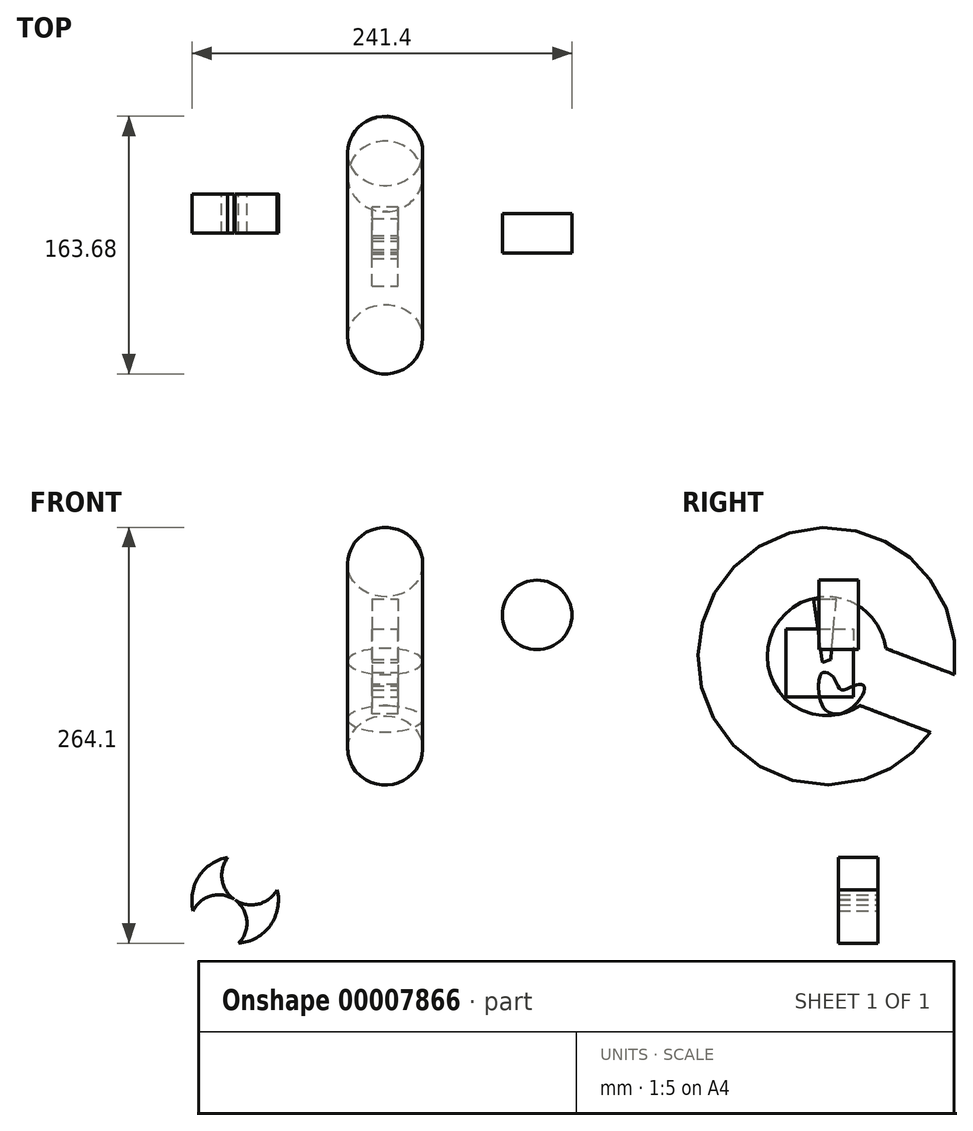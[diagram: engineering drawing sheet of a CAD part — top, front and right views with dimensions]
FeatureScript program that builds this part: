
annotation { "Feature Type Name" : "Feature", "Feature Type Description" : "" }
export const myFeature = defineFeature(function(context is Context, id is Id, definition is map)
    precondition{}
    {
        {
            var Q0;
            Q0=qCreatedBy(makeId("Right.planeOp"),FACE);
            var sketch = newSketch(context, id + "F0", { "sketchPlane" : qUnion([Q0])});
            skLineSegment(sketch, "E0", {"start": v(19.95, -37.15) * mm, "end": v(-30.55, -17.84) * mm});
            skLineSegment(sketch, "E1", {"start": v(-30.55, -17.84) * mm, "end": v(-20, 20.6) * mm});
            skLineSegment(sketch, "E2", {"start": v(-20, 20.6) * mm, "end": v(30.51, 1.3) * mm});
            skLineSegment(sketch, "E3", {"start": v(30.51, 1.3) * mm, "end": v(19.95, -37.15) * mm});
            skSolve(sketch);
        }
        {
            var Q0;
            Q0=makeQuery(id+"F0.imprint","IMPRINT",FACE,{"disambiguationData":[TD([[makeQuery(id+"F0.imprint","IMPRINT",EDGE,{"derivedFrom":sQuery(id+"F0.wireOp",EDGE,"E0")}),-1.0]])]});
            extrude(context, id + "F1", {"entities" : qUnion([Q0]), "depth" : 50.8 * mm});
        }
        {
            var Q0;
            Q0=qCreatedBy(makeId("Top.planeOp"),FACE);
            var sketch = newSketch(context, id + "F2", { "sketchPlane" : qUnion([Q0])});
            skCircle(sketch, "E4", {"center": v(-26.99, 35.44) * mm, "radius": 23.77 * mm});
            skSolve(sketch);
        }
        {
            var Q0;
            Q0=makeQuery(id+"F2.imprint","IMPRINT",FACE,{"disambiguationData":[TD([[makeQuery(id+"F2.imprint","IMPRINT",EDGE,{"derivedFrom":sQuery(id+"F2.wireOp",EDGE,"E4")}),1.0]])]});
            var Q1;
            Q1=makeQuery(id+"F1.opExtrude","SWEPT_EDGE",EDGE,{"disambiguationData":[OSD([sQuery(id+"F0.wireOp",EDGE,"E1"),sQuery(id+"F0.wireOp",EDGE,"E2")])]});
            revolve(context, id + "F3", {"entities" : qUnion([Q0]), "axis" : qUnion([Q1]), "revolveType" : RevolveType.FULL});
        }
        {
            var Q0;
            Q0=makeQuery(id+"F1.opExtrude","SWEPT_BODY",BODY,{"disambiguationData":[OSD([sQuery(id+"F0.wireOp",EDGE,"E0"),sQuery(id+"F0.wireOp",EDGE,"E1"),sQuery(id+"F0.wireOp",EDGE,"E2"),sQuery(id+"F0.wireOp",EDGE,"E3")])]});
            var Q1;
            Q1=sQuery(id+"F0.wireOp",VERTEX,"E0.start");
            var Q2;
            Q2=makeQuery(id+"F1.opExtrude","CAP_VERTEX",VERTEX,{"disambiguationData":[OSD([sQuery(id+"F0.wireOp",EDGE,"E1"),sQuery(id+"F0.wireOp",EDGE,"E2")])],"isStart":false});
            transform(context, id + "F4", {"entities" : qUnion([Q0]), "transformType" : TransformType.TRANSLATION_ENTITY, "oppositeDirectionEntity" : true, "transformLine" : qUnion([Q1, Q2]), "makeCopy" : false});
        }
        {
            var Q0;
            Q0=makeQuery(id+"F1.opExtrude","SWEPT_BODY",BODY,{"disambiguationData":[OSD([sQuery(id+"F0.wireOp",EDGE,"E0"),sQuery(id+"F0.wireOp",EDGE,"E1"),sQuery(id+"F0.wireOp",EDGE,"E2"),sQuery(id+"F0.wireOp",EDGE,"E3")])]});
            var Q1;
            Q1=makeQuery(id+"F1.opExtrude","CAP_VERTEX",VERTEX,{"disambiguationData":[OSD([sQuery(id+"F0.wireOp",EDGE,"E0"),sQuery(id+"F0.wireOp",EDGE,"E3")])],"isStart":true});
            var Q2;
            Q2=makeQuery(id+"F1.opExtrude","CAP_VERTEX",VERTEX,{"disambiguationData":[OSD([sQuery(id+"F0.wireOp",EDGE,"E1"),sQuery(id+"F0.wireOp",EDGE,"E2")])],"isStart":true});
            transform(context, id + "F5", {"entities" : qUnion([Q0]), "transformType" : TransformType.TRANSLATION_ENTITY, "oppositeDirectionEntity" : false, "transformLine" : qUnion([Q1, Q2]), "makeCopy" : false});
        }
        {
            var Q0;
            Q0=makeQuery(id+"F1.opExtrude","SWEPT_BODY",BODY,{"disambiguationData":[OSD([sQuery(id+"F0.wireOp",EDGE,"E0"),sQuery(id+"F0.wireOp",EDGE,"E1"),sQuery(id+"F0.wireOp",EDGE,"E2"),sQuery(id+"F0.wireOp",EDGE,"E3")])]});
            transform(context, id + "F6", {"entities" : qUnion([Q0]), "transformType" : TransformType.TRANSLATION_3D, "dx" : 0 * mm, "dy" : 31.82 * mm, "dz" : 7.18 * mm, "makeCopy" : false});
        }
        {
            var Q0;
            Q0=makeQuery(id+"F1.opExtrude","SWEPT_BODY",BODY,{"disambiguationData":[OSD([sQuery(id+"F0.wireOp",EDGE,"E0"),sQuery(id+"F0.wireOp",EDGE,"E1"),sQuery(id+"F0.wireOp",EDGE,"E2"),sQuery(id+"F0.wireOp",EDGE,"E3")])]});
            var Q1;
            Q1=makeQuery(id+"F3.opRevolve","SWEPT_BODY",BODY,{"disambiguationData":[OSD([sQuery(id+"F2.wireOp",EDGE,"E4")])]});
            booleanBodies(context, id + "F7", {"operationType" : BooleanOperationType.SUBTRACTION, "tools" : qUnion([Q0]), "targets" : qUnion([Q1])});
        }
        {
            var Q0;
            Q0=qCreatedBy(makeId("Front.planeOp"),FACE);
            var sketch = newSketch(context, id + "F8", { "sketchPlane" : qUnion([Q0])});
            skLineSegment(sketch, "E5", {"start": v(122.05, 43.72) * mm, "end": v(113.3, -18.18) * mm});
            skLineSegment(sketch, "E6", {"start": v(105.23, -15.49) * mm, "end": v(99.7, 43.72) * mm});
            skLineSegment(sketch, "E7", {"start": v(105.23, -15.49) * mm, "end": v(113.3, -18.18) * mm});
            skLineSegment(sketch, "E8", {"start": v(122.05, 43.72) * mm, "end": v(99.7, 43.72) * mm});
            skLineSegment(sketch, "E9.bottom", {"start": v(148.96, 14.45) * mm, "end": v(83.03, 14.45) * mm});
            skLineSegment(sketch, "E9.top", {"start": v(148.96, -51.82) * mm, "end": v(83.03, -51.82) * mm});
            skLineSegment(sketch, "E9.left", {"start": v(148.96, 14.45) * mm, "end": v(148.96, -51.82) * mm});
            skLineSegment(sketch, "E9.right", {"start": v(83.03, 14.45) * mm, "end": v(83.03, -51.82) * mm});
            skFitSpline(sketch, "E10", {"points": [v(117, -38.38) * mm, v(111.6, -63.46) * mm, v(89.21, -65.78) * mm, v(72.23, -42.62) * mm, v(79.18, -39.92) * mm, v(95, -44.94) * mm, v(102.72, -32.6) * mm, v(113.52, -28.35) * mm, v(116.22, -33.36) * mm, v(117, -38.38) * mm]});
            skSolve(sketch);
        }
        {
            var Q0;
            {var subQ5=sQuery(id+"F8.wireOp",EDGE,"E8");Q0=makeQuery(id+"F8.imprint","IMPRINT",FACE,{"disambiguationData":[TD([[makeQuery(id+"F8.imprint","IMPRINT",EDGE,{"derivedFrom":subQ5}),1.0]])]});}
            var Q1;
            {var subQ7=sQuery(id+"F8.wireOp",EDGE,"E7");Q1=makeQuery(id+"F8.imprint","IMPRINT",FACE,{"disambiguationData":[TD([[makeQuery(id+"F8.imprint","IMPRINT",EDGE,{"derivedFrom":subQ7}),-1.0]])]});}
            var Q2;
            {var subQ1=sQuery(id+"F8.wireOp",EDGE,"E9.right");var subQ3=sQuery(id+"F8.wireOp",EDGE,"E9.top");var subQ5=makeQuery(id+"F8.imprint","INTERSECT",VERTEX,{"derivedFrom":[subQ3,subQ1]});Q2=makeQuery(id+"F8.imprint","IMPRINT",FACE,{"disambiguationData":[TD([[makeQuery(id+"F8.imprint","IMPRINT",EDGE,{"disambiguationData":[TD([[subQ5,1.0]])],"derivedFrom":subQ3}),1.0]])]});}
            extrude(context, id + "F9", {"entities" : qUnion([Q0, Q1, Q2]), "depth" : 25.4 * mm});
        }
        {
            var Q0;
            Q0=makeQuery(id+"F9.opExtrude","SWEPT_BODY",BODY,{"disambiguationData":[OSD([sQuery(id+"F8.wireOp",EDGE,"E5"),sQuery(id+"F8.wireOp",EDGE,"E6"),sQuery(id+"F8.wireOp",EDGE,"E7"),sQuery(id+"F8.wireOp",EDGE,"E9.bottom"),sQuery(id+"F8.wireOp",EDGE,"E9.top"),sQuery(id+"F8.wireOp",EDGE,"E9.left"),sQuery(id+"F8.wireOp",EDGE,"E9.right"),sQuery(id+"F8.wireOp",EDGE,"E10")])]});
            var Q1;
            Q1=makeQuery(id+"F9.opExtrude","SWEPT_BODY",BODY,{"disambiguationData":[OSD([sQuery(id+"F8.wireOp",EDGE,"E9.top"),sQuery(id+"F8.wireOp",EDGE,"E9.right"),sQuery(id+"F8.wireOp",EDGE,"E10")])]});
            var Q2;
            Q2=makeQuery(id+"F9.opExtrude","SWEPT_BODY",BODY,{"disambiguationData":[OSD([sQuery(id+"F8.wireOp",EDGE,"E5"),sQuery(id+"F8.wireOp",EDGE,"E6"),sQuery(id+"F8.wireOp",EDGE,"E8"),sQuery(id+"F8.wireOp",EDGE,"E9.bottom")])]});
            var Q3;
            Q3=makeQuery(id+"F9.opExtrude","CAP_EDGE",EDGE,{"disambiguationData":[OSD([sQuery(id+"F8.wireOp",EDGE,"E9.left")])],"isStart":false});
            transform(context, id + "F10", {"entities" : qUnion([Q0, Q1, Q2]), "transformType" : TransformType.ROTATION, "transformAxis" : qUnion([Q3]), "angle" : 90 * degree, "makeCopy" : false});
        }
        {
            var Q0;
            Q0=makeQuery(id+"F9.opExtrude","SWEPT_BODY",BODY,{"disambiguationData":[OSD([sQuery(id+"F8.wireOp",EDGE,"E9.top"),sQuery(id+"F8.wireOp",EDGE,"E9.right"),sQuery(id+"F8.wireOp",EDGE,"E10")])]});
            var Q1;
            Q1=makeQuery(id+"F9.opExtrude","SWEPT_BODY",BODY,{"disambiguationData":[OSD([sQuery(id+"F8.wireOp",EDGE,"E5"),sQuery(id+"F8.wireOp",EDGE,"E6"),sQuery(id+"F8.wireOp",EDGE,"E7"),sQuery(id+"F8.wireOp",EDGE,"E9.bottom"),sQuery(id+"F8.wireOp",EDGE,"E9.top"),sQuery(id+"F8.wireOp",EDGE,"E9.left"),sQuery(id+"F8.wireOp",EDGE,"E9.right"),sQuery(id+"F8.wireOp",EDGE,"E10")])]});
            var Q2;
            Q2=makeQuery(id+"F9.opExtrude","SWEPT_BODY",BODY,{"disambiguationData":[OSD([sQuery(id+"F8.wireOp",EDGE,"E5"),sQuery(id+"F8.wireOp",EDGE,"E6"),sQuery(id+"F8.wireOp",EDGE,"E8"),sQuery(id+"F8.wireOp",EDGE,"E9.bottom")])]});
            transform(context, id + "F11", {"entities" : qUnion([Q0, Q1, Q2]), "transformType" : TransformType.TRANSLATION_3D, "dx" : 0 * mm, "dy" : -32.97 * mm, "dz" : 32.3 * mm, "makeCopy" : false});
        }
        {
            var Q0;
            Q0=makeQuery(id+"F9.opExtrude","SWEPT_BODY",BODY,{"disambiguationData":[OSD([sQuery(id+"F8.wireOp",EDGE,"E9.top"),sQuery(id+"F8.wireOp",EDGE,"E9.right"),sQuery(id+"F8.wireOp",EDGE,"E10")])]});
            var Q1;
            Q1=makeQuery(id+"F9.opExtrude","SWEPT_BODY",BODY,{"disambiguationData":[OSD([sQuery(id+"F8.wireOp",EDGE,"E5"),sQuery(id+"F8.wireOp",EDGE,"E6"),sQuery(id+"F8.wireOp",EDGE,"E7"),sQuery(id+"F8.wireOp",EDGE,"E9.bottom"),sQuery(id+"F8.wireOp",EDGE,"E9.top"),sQuery(id+"F8.wireOp",EDGE,"E9.left"),sQuery(id+"F8.wireOp",EDGE,"E9.right"),sQuery(id+"F8.wireOp",EDGE,"E10")])]});
            var Q2;
            Q2=makeQuery(id+"F9.opExtrude","SWEPT_BODY",BODY,{"disambiguationData":[OSD([sQuery(id+"F8.wireOp",EDGE,"E5"),sQuery(id+"F8.wireOp",EDGE,"E6"),sQuery(id+"F8.wireOp",EDGE,"E8"),sQuery(id+"F8.wireOp",EDGE,"E9.bottom")])]});
            var Q3;
            Q3=makeQuery(id+"F9.opExtrude","CAP_VERTEX",VERTEX,{"disambiguationData":[OSD([sQuery(id+"F8.wireOp",EDGE,"E5"),sQuery(id+"F8.wireOp",EDGE,"E7")])],"isStart":true});
            transform(context, id + "F12", {"entities" : qUnion([Q0, Q1, Q2]), "transformType" : TransformType.SCALE_UNIFORMLY, "scale" : 0.65, "makeCopy" : false, "scalePoint" : qUnion([Q3])});
        }
        {
            var Q0;
            Q0=makeQuery(id+"F9.opExtrude","SWEPT_BODY",BODY,{"disambiguationData":[OSD([sQuery(id+"F8.wireOp",EDGE,"E9.top"),sQuery(id+"F8.wireOp",EDGE,"E9.right"),sQuery(id+"F8.wireOp",EDGE,"E10")])]});
            var Q1;
            Q1=makeQuery(id+"F9.opExtrude","SWEPT_BODY",BODY,{"disambiguationData":[OSD([sQuery(id+"F8.wireOp",EDGE,"E5"),sQuery(id+"F8.wireOp",EDGE,"E6"),sQuery(id+"F8.wireOp",EDGE,"E7"),sQuery(id+"F8.wireOp",EDGE,"E9.bottom"),sQuery(id+"F8.wireOp",EDGE,"E9.top"),sQuery(id+"F8.wireOp",EDGE,"E9.left"),sQuery(id+"F8.wireOp",EDGE,"E9.right"),sQuery(id+"F8.wireOp",EDGE,"E10")])]});
            var Q2;
            Q2=makeQuery(id+"F9.opExtrude","SWEPT_BODY",BODY,{"disambiguationData":[OSD([sQuery(id+"F8.wireOp",EDGE,"E5"),sQuery(id+"F8.wireOp",EDGE,"E6"),sQuery(id+"F8.wireOp",EDGE,"E8"),sQuery(id+"F8.wireOp",EDGE,"E9.bottom")])]});
            transform(context, id + "F13", {"entities" : qUnion([Q0, Q1, Q2]), "transformType" : TransformType.TRANSLATION_3D, "dx" : 0 * mm, "dy" : 0 * mm, "dz" : 2.7 * mm, "makeCopy" : false});
        }
        {
            var Q0;
            Q0=makeQuery(id+"F9.opExtrude","SWEPT_BODY",BODY,{"disambiguationData":[OSD([sQuery(id+"F8.wireOp",EDGE,"E9.top"),sQuery(id+"F8.wireOp",EDGE,"E9.right"),sQuery(id+"F8.wireOp",EDGE,"E10")])]});
            var Q1;
            Q1=makeQuery(id+"F9.opExtrude","SWEPT_BODY",BODY,{"disambiguationData":[OSD([sQuery(id+"F8.wireOp",EDGE,"E5"),sQuery(id+"F8.wireOp",EDGE,"E6"),sQuery(id+"F8.wireOp",EDGE,"E8"),sQuery(id+"F8.wireOp",EDGE,"E9.bottom")])]});
            var Q2;
            Q2=makeQuery(id+"F9.opExtrude","SWEPT_BODY",BODY,{"disambiguationData":[OSD([sQuery(id+"F8.wireOp",EDGE,"E5"),sQuery(id+"F8.wireOp",EDGE,"E6"),sQuery(id+"F8.wireOp",EDGE,"E7"),sQuery(id+"F8.wireOp",EDGE,"E9.bottom"),sQuery(id+"F8.wireOp",EDGE,"E9.top"),sQuery(id+"F8.wireOp",EDGE,"E9.left"),sQuery(id+"F8.wireOp",EDGE,"E9.right"),sQuery(id+"F8.wireOp",EDGE,"E10")])]});
            var Q3;
            {var subQ0=sQuery(id+"F8.wireOp",EDGE,"E9.right");var subQ1=sQuery(id+"F8.wireOp",EDGE,"E10");Q3=makeQuery(id+"F9.opExtrude","CAP_VERTEX",VERTEX,{"disambiguationData":[OSD([subQ0,subQ1]),ownerDisambiguation([makeQuery(id+"F9.opExtrude","SWEPT_BODY",BODY,{"disambiguationData":[OSD([sQuery(id+"F8.wireOp",EDGE,"E5"),sQuery(id+"F8.wireOp",EDGE,"E6"),sQuery(id+"F8.wireOp",EDGE,"E7"),sQuery(id+"F8.wireOp",EDGE,"E9.bottom"),sQuery(id+"F8.wireOp",EDGE,"E9.top"),sQuery(id+"F8.wireOp",EDGE,"E9.left"),subQ0,subQ1])]})])],"isStart":false});}
            transform(context, id + "F14", {"entities" : qUnion([Q0, Q1, Q2]), "transformType" : TransformType.TRANSLATION_3D, "dx" : -191.07 * mm, "dy" : 0 * mm, "dz" : 0 * mm, "makeCopy" : false});
        }
        {
            var Q0;
            Q0=makeQuery(id+"F9.opExtrude","SWEPT_BODY",BODY,{"disambiguationData":[OSD([sQuery(id+"F8.wireOp",EDGE,"E5"),sQuery(id+"F8.wireOp",EDGE,"E6"),sQuery(id+"F8.wireOp",EDGE,"E7"),sQuery(id+"F8.wireOp",EDGE,"E9.bottom"),sQuery(id+"F8.wireOp",EDGE,"E9.top"),sQuery(id+"F8.wireOp",EDGE,"E9.left"),sQuery(id+"F8.wireOp",EDGE,"E9.right"),sQuery(id+"F8.wireOp",EDGE,"E10")])]});
            var Q1;
            Q1=makeQuery(id+"F9.opExtrude","SWEPT_BODY",BODY,{"disambiguationData":[OSD([sQuery(id+"F8.wireOp",EDGE,"E5"),sQuery(id+"F8.wireOp",EDGE,"E6"),sQuery(id+"F8.wireOp",EDGE,"E8"),sQuery(id+"F8.wireOp",EDGE,"E9.bottom")])]});
            var Q2;
            Q2=makeQuery(id+"F9.opExtrude","SWEPT_BODY",BODY,{"disambiguationData":[OSD([sQuery(id+"F8.wireOp",EDGE,"E9.top"),sQuery(id+"F8.wireOp",EDGE,"E9.right"),sQuery(id+"F8.wireOp",EDGE,"E10")])]});
            transform(context, id + "F15", {"entities" : qUnion([Q0, Q1, Q2]), "transformType" : TransformType.TRANSLATION_3D, "dx" : -2.02 * mm, "dy" : 0 * mm, "dz" : 0 * mm, "makeCopy" : false});
        }
        {
            var Q0;
            Q0=qCreatedBy(makeId("Front.planeOp"),FACE);
            var sketch = newSketch(context, id + "F16", { "sketchPlane" : qUnion([Q0])});
            skEllipse(sketch, "E11", {"center": v(132.43, 37.26) * mm, "majorRadius": 10 * mm, "minorRadius": 6.2 * mm, "majorAxis": v(-0.77, 0.64)});
            skCircle(sketch, "E12", {"center": v(69.53, 46.9) * mm, "radius": 12.85 * mm});
            skCircle(sketch, "E13", {"center": v(69.53, 46.9) * mm, "radius": 22.07 * mm});
            skArc(sketch, "E14", {"start": v(-10.98, -133.24) * mm, "mid": v(4.84, -158.05) * mm, "end": v(34.14, -155.42) * mm});
            skArc(sketch, "E15", {"start": v(34.14, -155.42) * mm, "mid": v(29.82, -107.24) * mm, "end": v(-10.98, -133.24) * mm});
            skLineSegment(sketch, "E16", {"start": v(-10.98, -133.24) * mm, "end": v(34.14, -155.42) * mm});
            skLineSegment(sketch, "E17", {"start": v(17.33, -104.33) * mm, "end": v(17.33, -132.64) * mm});
            skLineSegment(sketch, "E18", {"start": v(17.33, -132.64) * mm, "end": v(42.01, -146.51) * mm});
            skArc(sketch, "E19.0", {"start": v(-22.97, -133.49) * mm, "mid": v(-0.46, -168.82) * mm, "end": v(41.27, -165.08) * mm});
            skLineSegment(sketch, "E20", {"start": v(-10.98, -133.24) * mm, "end": v(-22.97, -133.49) * mm});
            skLineSegment(sketch, "E21", {"start": v(34.14, -155.42) * mm, "end": v(41.27, -165.08) * mm});
            skSolve(sketch);
        }
        {
            var Q0;
            Q0=makeQuery(id+"F16.imprint","IMPRINT",FACE,{"disambiguationData":[TD([[makeQuery(id+"F16.imprint","IMPRINT",EDGE,{"derivedFrom":sQuery(id+"F16.wireOp",EDGE,"E12")}),1.0]])]});
            var Q1;
            Q1=makeQuery(id+"F16.imprint","IMPRINT",FACE,{"disambiguationData":[TD([[makeQuery(id+"F16.imprint","IMPRINT",EDGE,{"derivedFrom":sQuery(id+"F16.wireOp",EDGE,"E12")}),-1.0]])]});
            var Q2;
            Q2=sQuery(id+"F16.wireOp",EDGE,"E13");
            var Q3;
            Q3=sQuery(id+"F16.wireOp",EDGE,"E12");
            extrude(context, id + "F17", {"entities" : qUnion([Q0, Q1]), "surfaceEntities" : qUnion([Q2, Q3]), "depth" : 25 * mm});
        }
        {
            var Q0;
            Q0=qCreatedBy(makeId("Front.planeOp"),FACE);
            var sketch = newSketch(context, id + "F18", { "sketchPlane" : qUnion([Q0])});
            skCircle(sketch, "E22", {"center": v(-112.01, -118.53) * mm, "radius": 18.79 * mm});
            skArc(sketch, "E23", {"start": v(-126.96, -107.15) * mm, "mid": v(-137.35, -157.26) * mm, "end": v(-95.6, -127.67) * mm});
            skArc(sketch, "E24", {"start": v(-120.02, -161.66) * mm, "mid": v(-122.3, -134.25) * mm, "end": v(-148.96, -140.97) * mm});
            skLineSegment(sketch, "E25", {"start": v(-112.01, -118.53) * mm, "end": v(-112.01, -98.92) * mm, "construction": true});
            skSolve(sketch);
        }
        {
            var Q0;
            {var subQ1=sQuery(id+"F18.wireOp",EDGE,"E22");var subQ3=sQuery(id+"F18.wireOp",EDGE,"E23");var subQ5=makeQuery(id+"F18.imprint","INTERSECT",VERTEX,{"disambiguationData":[OD(0.0)],"derivedFrom":[subQ1,subQ3]});Q0=makeQuery(id+"F18.imprint","IMPRINT",FACE,{"disambiguationData":[TD([[makeQuery(id+"F18.imprint","IMPRINT",EDGE,{"disambiguationData":[TD([[subQ5,-1.0]])],"derivedFrom":subQ1}),-1.0]])]});}
            var Q1;
            {var subQ1=sQuery(id+"F18.wireOp",EDGE,"E22");var subQ3=sQuery(id+"F18.wireOp",EDGE,"E23");var subQ5=makeQuery(id+"F18.imprint","INTERSECT",VERTEX,{"disambiguationData":[OD(1.0)],"derivedFrom":[subQ1,subQ3]});Q1=makeQuery(id+"F18.imprint","IMPRINT",FACE,{"disambiguationData":[TD([[makeQuery(id+"F18.imprint","IMPRINT",EDGE,{"disambiguationData":[TD([[subQ5,1.0]])],"derivedFrom":subQ1}),-1.0]])]});}
            extrude(context, id + "F19", {"entities" : qUnion([Q0, Q1]), "endBound" : BoundingType.SYMMETRIC, "depth" : 25 * mm});
        }
    });
